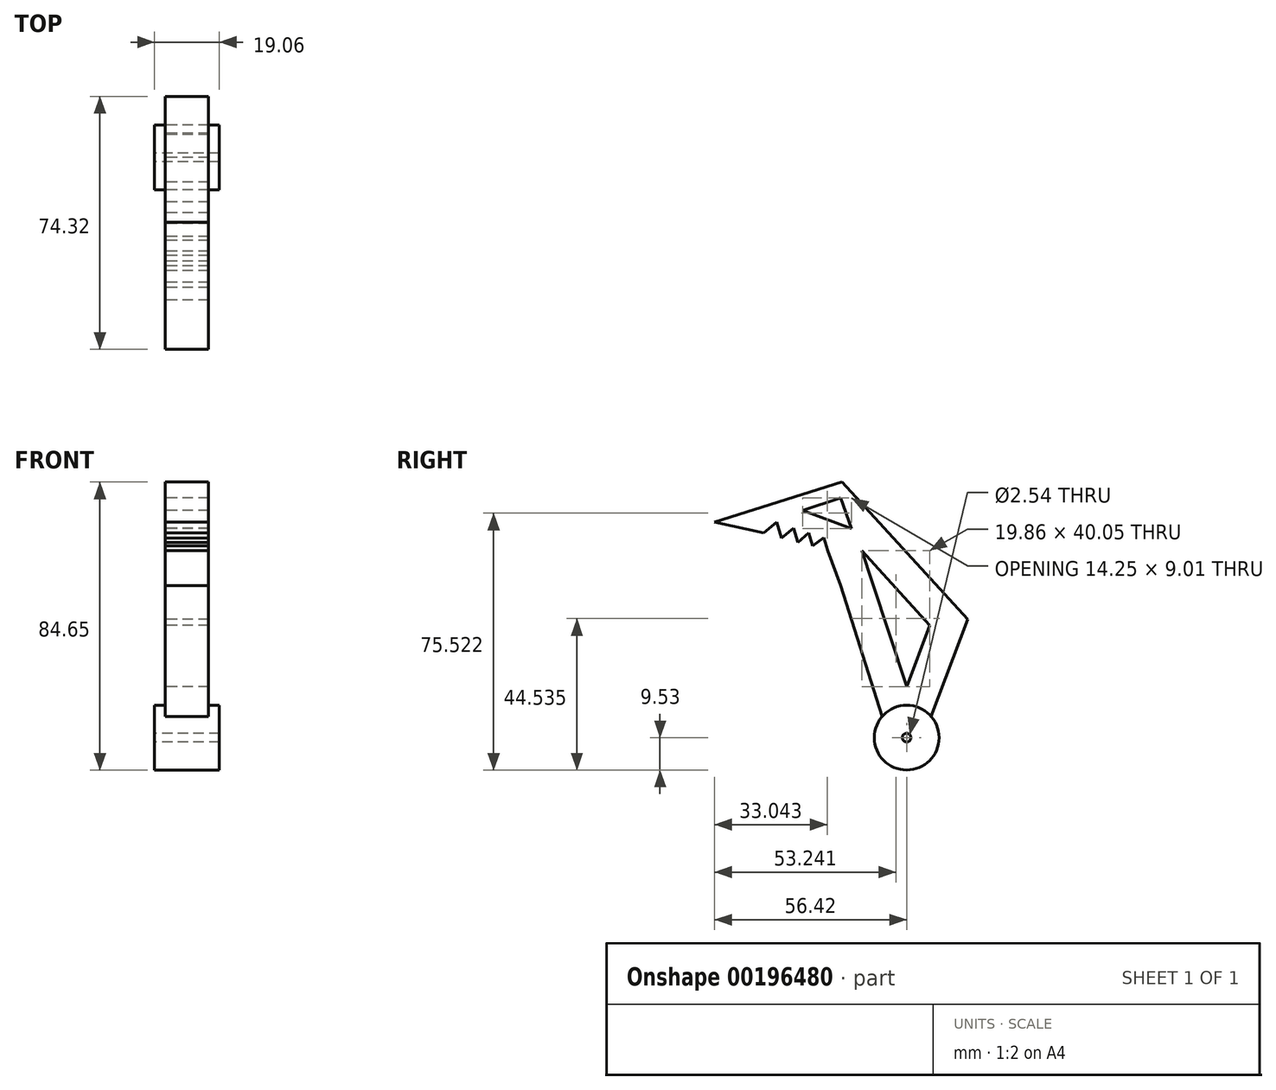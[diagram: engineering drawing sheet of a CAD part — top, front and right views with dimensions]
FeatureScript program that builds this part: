
annotation { "Feature Type Name" : "Feature", "Feature Type Description" : "" }
export const myFeature = defineFeature(function(context is Context, id is Id, definition is map)
    precondition{}
    {
        {
            var Q0;
            Q0=qCreatedBy(makeId("Right.planeOp"),FACE);
            var sketch = newSketch(context, id + "F0", { "sketchPlane" : qUnion([Q0])});
            skCircle(sketch, "E0", {"center": v(0, 0) * mm, "radius": 9.53 * mm});
            skCircle(sketch, "E1", {"center": v(0, 0) * mm, "radius": 1.27 * mm});
            skLineSegment(sketch, "E2", {"start": v(7.18, 6.26) * mm, "end": v(13.83, 23.96) * mm});
            skLineSegment(sketch, "E3", {"start": v(-19.4, 44.64) * mm, "end": v(-7.2, 6.24) * mm});
            skLineSegment(sketch, "E4", {"start": v(13.83, 23.96) * mm, "end": v(17.9, 34.8) * mm});
            skLineSegment(sketch, "E5", {"start": v(17.9, 34.8) * mm, "end": v(-19, 75.12) * mm});
            skLineSegment(sketch, "E6", {"start": v(-19, 75.12) * mm, "end": v(-56.42, 63.4) * mm});
            skPoint(sketch, "E7.start.orphan", {"position": v(0, 14.98) * mm});
            skPoint(sketch, "E8.start.orphan", {"position": v(-24.56, 45.66) * mm});
            skPoint(sketch, "E9.end.orphan", {"position": v(-28.2, 47.3) * mm});
            skPoint(sketch, "E10.end.orphan", {"position": v(-32.04, 45.66) * mm});
            skPoint(sketch, "E10.start.orphan", {"position": v(-41.25, 47.3) * mm});
            skLineSegment(sketch, "E11", {"start": v(-56.42, 63.4) * mm, "end": v(-41.95, 60.15) * mm});
            skLineSegment(sketch, "E12", {"start": v(-41.95, 60.15) * mm, "end": v(-38.2, 63.4) * mm});
            skLineSegment(sketch, "E13", {"start": v(-38.2, 63.4) * mm, "end": v(-36.73, 58.67) * mm});
            skLineSegment(sketch, "E14", {"start": v(-36.73, 58.67) * mm, "end": v(-33.2, 61.61) * mm});
            skLineSegment(sketch, "E15", {"start": v(-33.2, 61.61) * mm, "end": v(-31.9, 57.45) * mm});
            skLineSegment(sketch, "E16", {"start": v(-31.9, 57.45) * mm, "end": v(-28.8, 60.15) * mm});
            skLineSegment(sketch, "E17", {"start": v(-28.8, 60.15) * mm, "end": v(-27.61, 56.36) * mm});
            skLineSegment(sketch, "E18", {"start": v(-27.61, 56.36) * mm, "end": v(-24.39, 58.79) * mm});
            skLineSegment(sketch, "E19", {"start": v(-24.39, 58.79) * mm, "end": v(-23.2, 55.03) * mm});
            skLineSegment(sketch, "E20", {"start": v(-23.2, 55.03) * mm, "end": v(-19.4, 44.64) * mm});
            skLineSegment(sketch, "E21", {"start": v(-10.1, 45.66) * mm, "end": v(0, 14.98) * mm});
            skLineSegment(sketch, "E22", {"start": v(0, 14.98) * mm, "end": v(6.75, 32.95) * mm});
            skLineSegment(sketch, "E23", {"start": v(6.75, 32.95) * mm, "end": v(-13.11, 55.03) * mm});
            skLineSegment(sketch, "E24", {"start": v(-13.11, 55.03) * mm, "end": v(-10.1, 45.66) * mm});
            skLineSegment(sketch, "E25", {"start": v(-19.4, 70.5) * mm, "end": v(-30.5, 66.84) * mm});
            skLineSegment(sketch, "E26", {"start": v(-30.5, 66.84) * mm, "end": v(-16.25, 61.49) * mm});
            skLineSegment(sketch, "E27", {"start": v(-16.25, 61.49) * mm, "end": v(-19.4, 70.5) * mm});
            skSolve(sketch);
        }
        {
            var Q0;
            Q0=makeQuery(id+"F0.imprint","IMPRINT",FACE,{"disambiguationData":[TD([[makeQuery(id+"F0.imprint","IMPRINT",EDGE,{"derivedFrom":sQuery(id+"F0.wireOp",EDGE,"E1")}),-1.0]])]});
            extrude(context, id + "F1", {"entities" : qUnion([Q0]), "endBound" : BoundingType.SYMMETRIC, "depth" : 19.05 * mm});
        }
        {
            var Q0;
            {var subQ0=sQuery(id+"F0.wireOp",EDGE,"E2");Q0=makeQuery(id+"F0.imprint","IMPRINT",FACE,{"disambiguationData":[TD([[makeQuery(id+"F0.imprint","IMPRINT",EDGE,{"derivedFrom":subQ0}),1.0]])]});}
            extrude(context, id + "F2", {"entities" : qUnion([Q0]), "operationType" : NewBodyOperationType.ADD, "endBound" : BoundingType.SYMMETRIC, "depth" : 12.7 * mm});
        }
    });
